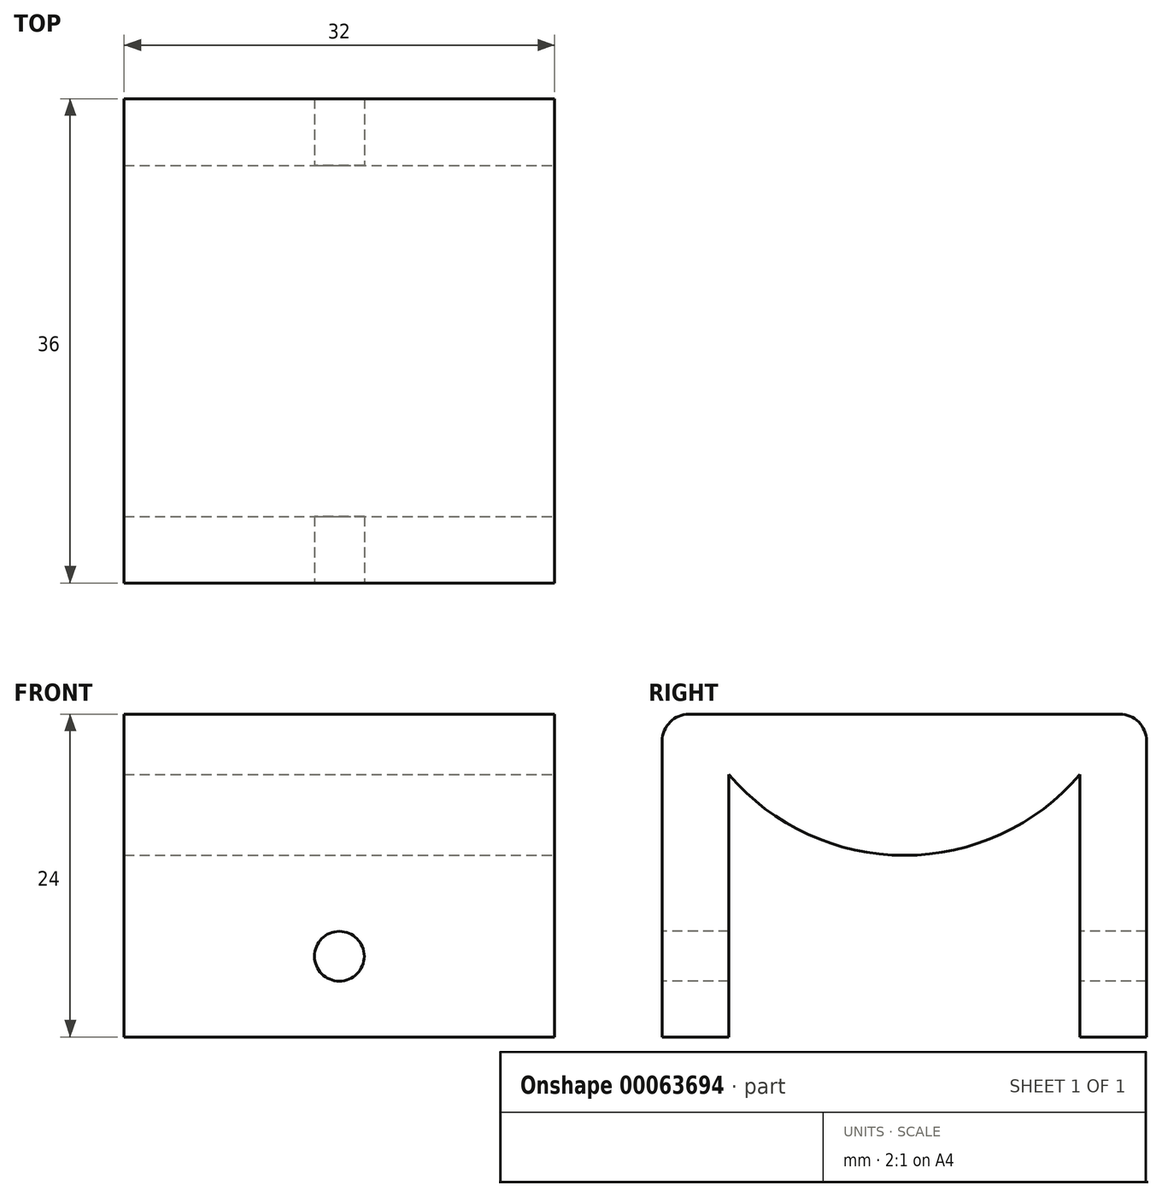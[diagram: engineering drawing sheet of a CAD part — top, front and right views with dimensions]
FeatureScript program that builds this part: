
annotation { "Feature Type Name" : "Feature", "Feature Type Description" : "" }
export const myFeature = defineFeature(function(context is Context, id is Id, definition is map)
    precondition{}
    {
        {
            var Q0;
            Q0=qCreatedBy(makeId("Top.planeOp"),FACE);
            var sketch = newSketch(context, id + "F0", { "sketchPlane" : qUnion([Q0])});
            skLineSegment(sketch, "E0.rect.bottom", {"start": v(-16, -18) * mm, "end": v(16, -18) * mm});
            skLineSegment(sketch, "E0.rect.top", {"start": v(-16, 18) * mm, "end": v(16, 18) * mm});
            skLineSegment(sketch, "E0.rect.left", {"start": v(-16, -18) * mm, "end": v(-16, 18) * mm});
            skLineSegment(sketch, "E0.rect.right", {"start": v(16, -18) * mm, "end": v(16, 18) * mm});
            skPoint(sketch, "E0.rect.middle", {"position": v(0, 0) * mm});
            skSolve(sketch);
        }
        {
            var Q0;
            Q0=makeQuery(id+"F0.imprint","IMPRINT",FACE,{"disambiguationData":[TD([[makeQuery(id+"F0.imprint","IMPRINT",EDGE,{"derivedFrom":sQuery(id+"F0.wireOp",EDGE,"E0.rect.bottom")}),1.0]])]});
            extrude(context, id + "F1", {"entities" : qUnion([Q0]), "depth" : 24 * mm});
        }
        {
            var Q0;
            Q0=makeQuery(id+"F1.opExtrude","SWEPT_FACE",FACE,{"disambiguationData":[OSD([sQuery(id+"F0.wireOp",EDGE,"E0.rect.right")])]});
            var sketch = newSketch(context, id + "F2", { "sketchPlane" : qUnion([Q0])});
            skLineSegment(sketch, "E1", {"start": v(0, 0) * mm, "end": v(0, 13.5) * mm, "construction": true});
            skLineSegment(sketch, "E2", {"start": v(0, 13.5) * mm, "end": v(0, 19.5) * mm, "construction": true});
            skLineSegment(sketch, "E3", {"start": v(0, 13.5) * mm, "end": v(-13.05, 13.5) * mm, "construction": true});
            skLineSegment(sketch, "E4", {"start": v(0, 13.5) * mm, "end": v(13.05, 13.5) * mm, "construction": true});
            skArc(sketch, "E5", {"start": v(-13.05, 19.5) * mm, "mid": v(0, 13.5) * mm, "end": v(13.05, 19.5) * mm});
            skLineSegment(sketch, "E6", {"start": v(-13.05, 19.5) * mm, "end": v(-13.05, 0) * mm});
            skLineSegment(sketch, "E7", {"start": v(13.05, 19.5) * mm, "end": v(13.05, 0) * mm});
            skSolve(sketch);
        }
        {
            var Q0;
            Q0=makeQuery(id+"F2.imprint","IMPRINT",FACE,{"disambiguationData":[TD([[makeQuery(id+"F2.imprint","IMPRINT",EDGE,{"derivedFrom":sQuery(id+"F2.wireOp",EDGE,"104de7ef-4b8a-4c65-a2f1-22dcef27fbfd")}),1.0]])]});
            var Q1;
            Q1=makeQuery(id+"F2.imprint","IMPRINT",FACE,{"disambiguationData":[TD([[makeQuery(id+"F2.imprint","IMPRINT",EDGE,{"derivedFrom":sQuery(id+"F2.wireOp",EDGE,"E5")}),-1.0]])]});
            extrude(context, id + "F3", {"entities" : qUnion([Q0, Q1]), "operationType" : NewBodyOperationType.REMOVE, "oppositeDirection" : true, "depth" : 89 * mm});
        }
        {
            var Q0;
            Q0=makeQuery(id+"F1.opExtrude","CAP_EDGE",EDGE,{"disambiguationData":[OSD([sQuery(id+"F0.wireOp",EDGE,"E0.rect.bottom")])],"isStart":false});
            fillet(context, id + "F4", {"entities" : qUnion([Q0]), "radius" : 2 * mm, "tangentPropagation" : true, "allowEdgeOverflow" : false});
        }
        {
            var Q0;
            Q0=makeQuery(id+"F1.opExtrude","CAP_EDGE",EDGE,{"disambiguationData":[OSD([sQuery(id+"F0.wireOp",EDGE,"E0.rect.top")])],"isStart":false});
            fillet(context, id + "F5", {"entities" : qUnion([Q0]), "radius" : 2 * mm, "tangentPropagation" : true, "allowEdgeOverflow" : false});
        }
        {
            var Q0;
            Q0=makeQuery(id+"F1.opExtrude","SWEPT_FACE",FACE,{"disambiguationData":[OSD([sQuery(id+"F0.wireOp",EDGE,"E0.rect.bottom")])]});
            var sketch = newSketch(context, id + "F6", { "sketchPlane" : qUnion([Q0])});
            skLineSegment(sketch, "E8", {"start": v(0, 0) * mm, "end": v(0, 6) * mm, "construction": true});
            skPoint(sketch, "E8.endSnap0", {"position": v(0, 0) * mm});
            skCircle(sketch, "E9", {"center": v(0, 6) * mm, "radius": 1.85 * mm});
            skLineSegment(sketch, "E10", {"start": v(0, 6) * mm, "end": v(-24, 6) * mm, "construction": true});
            skCircle(sketch, "E11", {"center": v(-24, 6) * mm, "radius": 1.85 * mm});
            skCircle(sketch, "E12.MirrorC", {"center": v(24, 6) * mm, "radius": 1.85 * mm});
            skSolve(sketch);
        }
        {
            var Q0;
            Q0=makeQuery(id+"F6.imprint","IMPRINT",FACE,{"disambiguationData":[TD([[makeQuery(id+"F6.imprint","IMPRINT",EDGE,{"derivedFrom":sQuery(id+"F6.wireOp",EDGE,"E11")}),1.0]])]});
            var Q1;
            Q1=makeQuery(id+"F6.imprint","IMPRINT",FACE,{"disambiguationData":[TD([[makeQuery(id+"F6.imprint","IMPRINT",EDGE,{"derivedFrom":sQuery(id+"F6.wireOp",EDGE,"E9")}),1.0]])]});
            var Q2;
            Q2=makeQuery(id+"F6.imprint","IMPRINT",FACE,{"disambiguationData":[TD([[makeQuery(id+"F6.imprint","IMPRINT",EDGE,{"derivedFrom":sQuery(id+"F6.wireOp",EDGE,"E12.MirrorC")}),-1.0]])]});
            extrude(context, id + "F7", {"entities" : qUnion([Q0, Q1, Q2]), "operationType" : NewBodyOperationType.REMOVE, "oppositeDirection" : true, "depth" : 90 * mm});
        }
    });
